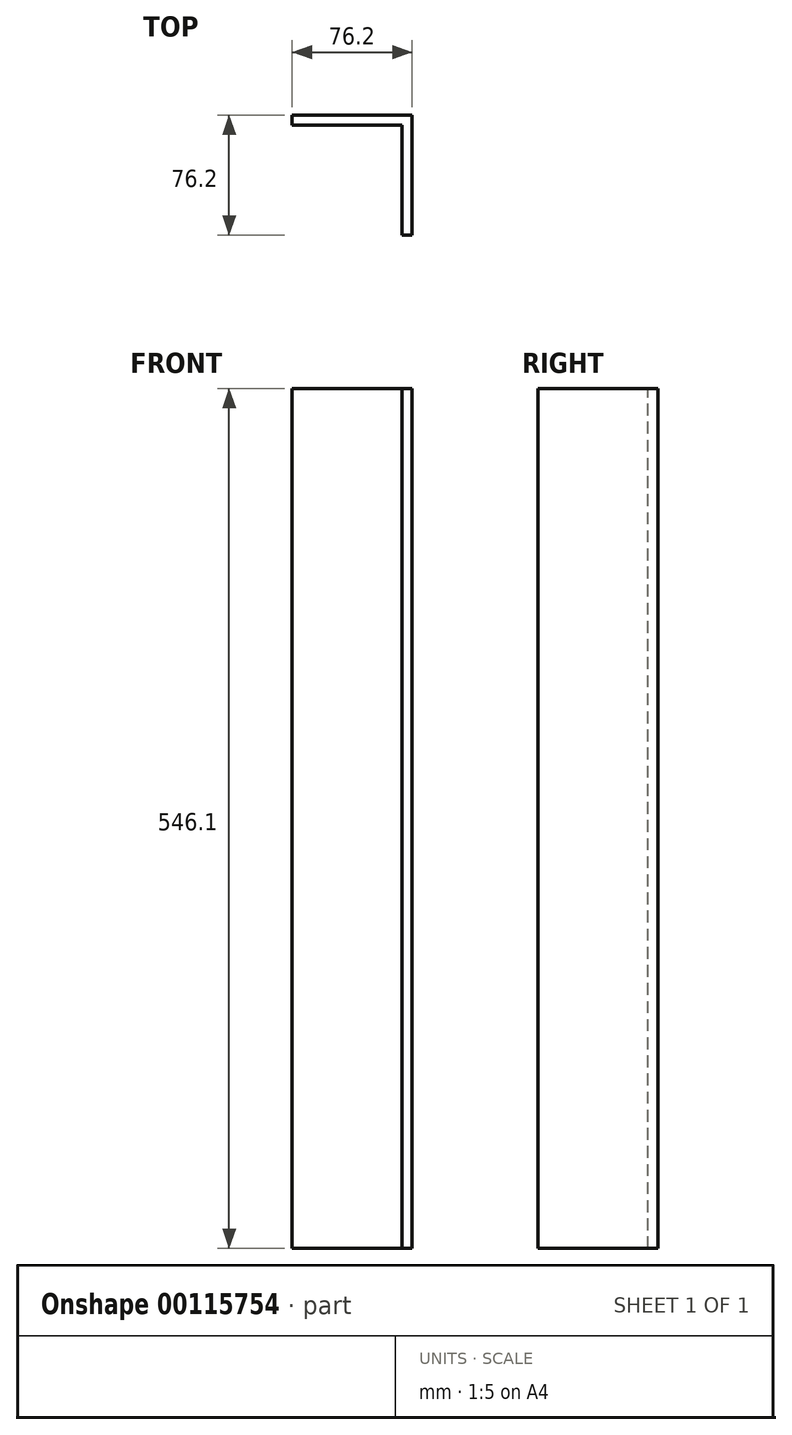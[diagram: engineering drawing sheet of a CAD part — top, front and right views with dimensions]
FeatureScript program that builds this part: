
annotation { "Feature Type Name" : "Feature", "Feature Type Description" : "" }
export const myFeature = defineFeature(function(context is Context, id is Id, definition is map)
    precondition{}
    {
        {
            var Q0;
            Q0=qCreatedBy(makeId("Top.planeOp"),FACE);
            var sketch = newSketch(context, id + "F0", { "sketchPlane" : qUnion([Q0])});
            skLineSegment(sketch, "E0", {"start": v(-76.2, 0) * mm, "end": v(0, 0) * mm});
            skLineSegment(sketch, "E1", {"start": v(0, 0) * mm, "end": v(0, -76.2) * mm});
            skLineSegment(sketch, "E2.0", {"start": v(-6.35, -6.35) * mm, "end": v(-6.35, -76.2) * mm});
            skLineSegment(sketch, "E2.1", {"start": v(-76.2, -6.35) * mm, "end": v(-6.35, -6.35) * mm});
            skLineSegment(sketch, "E3", {"start": v(-76.2, 0) * mm, "end": v(-76.2, -6.35) * mm});
            skLineSegment(sketch, "E4", {"start": v(-6.35, -76.2) * mm, "end": v(0, -76.2) * mm});
            skSolve(sketch);
        }
        {
            var Q0;
            Q0 = qSketchRegion(id + "F0", true);
            extrude(context, id + "F1", {"entities" : qUnion([Q0]), "oppositeDirection" : true, "depth" : 546.1 * mm});
        }
    });
